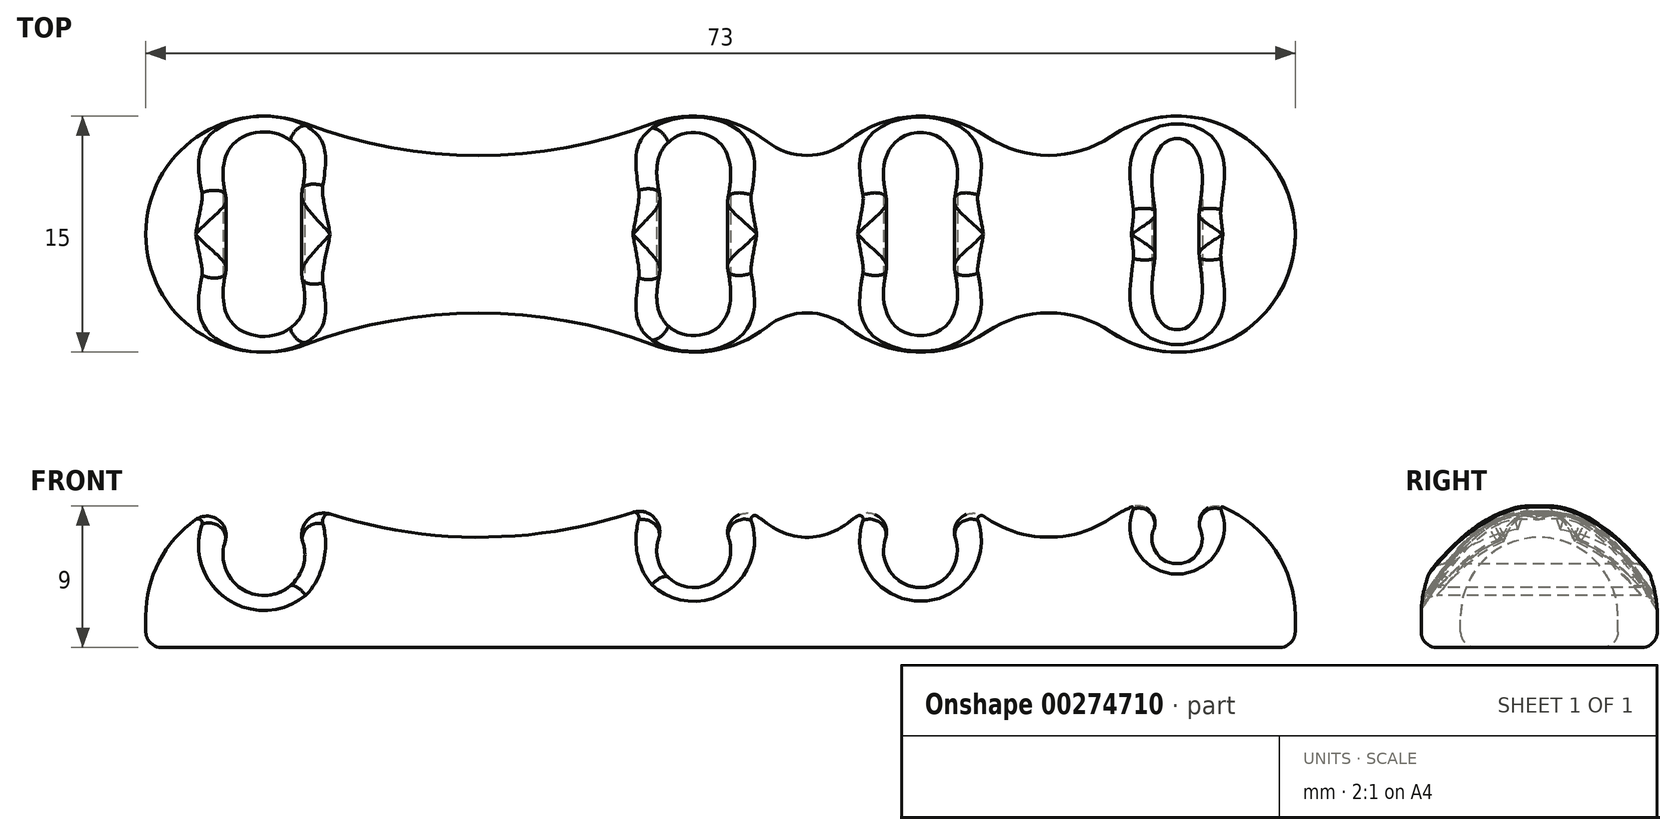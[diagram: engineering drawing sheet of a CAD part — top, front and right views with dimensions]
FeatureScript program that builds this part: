
annotation { "Feature Type Name" : "Feature", "Feature Type Description" : "" }
export const myFeature = defineFeature(function(context is Context, id is Id, definition is map)
    precondition{}
    {
        {
            var Q0;
            Q0=qCreatedBy(makeId("Top.planeOp"),FACE);
            var sketch = newSketch(context, id + "F0", { "sketchPlane" : qUnion([Q0])});
            skArc(sketch, "E0", {"start": v(7.5, 0) * mm, "mid": v(3.51, 6.63) * mm, "end": v(-4.2, 6.2) * mm});
            skArc(sketch, "E1", {"start": v(-55.34, 7.01) * mm, "mid": v(-62.26, 6.17) * mm, "end": v(-65.5, 0) * mm});
            skArc(sketch, "E2", {"start": v(-55.34, 7.01) * mm, "mid": v(-44.35, 5) * mm, "end": v(-33.36, 7.01) * mm});
            skArc(sketch, "E3", {"start": v(-26.05, 5.89) * mm, "mid": v(-23.5, 5) * mm, "end": v(-20.95, 5.89) * mm});
            skArc(sketch, "E4", {"start": v(-12.1, 6.2) * mm, "mid": v(-8.15, 5) * mm, "end": v(-4.2, 6.2) * mm});
            skLineSegment(sketch, "E5", {"start": v(-44.35, 5) * mm, "end": v(-8.15, 5) * mm, "construction": true});
            skLineSegment(sketch, "E6", {"start": v(-65.5, 0) * mm, "end": v(7.5, 0) * mm});
            skArc(sketch, "E7.trimOffspring", {"start": v(-26.05, 5.89) * mm, "mid": v(-29.56, 7.41) * mm, "end": v(-33.36, 7.01) * mm});
            skArc(sketch, "E8.trimOffspring", {"start": v(-12.1, 6.2) * mm, "mid": v(-16.57, 7.5) * mm, "end": v(-20.95, 5.89) * mm});
            skSolve(sketch);
        }
        {
            var Q0;
            Q0=makeQuery(id+"F0.imprint","IMPRINT",FACE,{"disambiguationData":[TD([[makeQuery(id+"F0.imprint","IMPRINT",EDGE,{"derivedFrom":sQuery(id+"F0.wireOp",EDGE,"E0")}),1.0]])]});
            var Q1;
            Q1=sQuery(id+"F0.wireOp",EDGE,"E6");
            revolve(context, id + "F1", {"entities" : qUnion([Q0]), "axis" : qUnion([Q1]), "revolveType" : RevolveType.ONE_DIRECTION, "angle" : 180 * degree});
        }
        {
            var Q0;
            Q0=makeQuery(id+"F1.opRevolve","CAP_FACE",FACE,{"disambiguationData":[OSD([sQuery(id+"F0.wireOp",EDGE,"E0"),sQuery(id+"F0.wireOp",EDGE,"E1"),sQuery(id+"F0.wireOp",EDGE,"E2"),sQuery(id+"F0.wireOp",EDGE,"E3"),sQuery(id+"F0.wireOp",EDGE,"E4"),sQuery(id+"F0.wireOp",EDGE,"E6"),sQuery(id+"F0.wireOp",EDGE,"E7.trimOffspring"),sQuery(id+"F0.wireOp",EDGE,"E8.trimOffspring")])],"isStart":true});
            extrude(context, id + "F2", {"entities" : qUnion([Q0]), "operationType" : NewBodyOperationType.ADD, "depth" : 2 * mm});
        }
        {
            var Q0;
            Q0=makeQuery(id+"F2.opExtrude","CAP_EDGE",EDGE,{"disambiguationData":[OSD([sQuery(id+"F0.wireOp",EDGE,"E1")])],"isStart":false});
            fillet(context, id + "F3", {"entities" : qUnion([Q0]), "radius" : 1 * mm, "tangentPropagation" : true, "allowEdgeOverflow" : false});
        }
        {
            var Q0;
            Q0=qCreatedBy(makeId("Front.planeOp"),FACE);
            var sketch = newSketch(context, id + "F4", { "sketchPlane" : qUnion([Q0])});
            skArc(sketch, "E9", {"start": v(-55.34, 7.01) * mm, "mid": v(-62.26, 6.17) * mm, "end": v(-65.5, 0) * mm});
            skArc(sketch, "E10", {"start": v(-26.05, 5.89) * mm, "mid": v(-29.56, 7.41) * mm, "end": v(-33.36, 7.01) * mm});
            skArc(sketch, "E11", {"start": v(-12.1, 6.2) * mm, "mid": v(-16.57, 7.5) * mm, "end": v(-20.95, 5.89) * mm});
            skArc(sketch, "E12", {"start": v(7.5, 0) * mm, "mid": v(3.51, 6.63) * mm, "end": v(-4.2, 6.2) * mm});
            skArc(sketch, "E13", {"start": v(-60.4, 4.9) * mm, "mid": v(-58, 1.3) * mm, "end": v(-55.6, 4.9) * mm});
            skArc(sketch, "E14", {"start": v(-32.85, 5.1) * mm, "mid": v(-30.7, 1.8) * mm, "end": v(-28.55, 5.1) * mm});
            skArc(sketch, "E15", {"start": v(-18.45, 5.1) * mm, "mid": v(-16.3, 1.8) * mm, "end": v(-14.15, 5.1) * mm});
            skArc(sketch, "E16", {"start": v(-1.4, 5.67) * mm, "mid": v(0, 3.3) * mm, "end": v(1.4, 5.67) * mm});
            skArc(sketch, "E17", {"start": v(-53.79, 6.47) * mm, "mid": v(-55.2, 6.13) * mm, "end": v(-55.53, 4.71) * mm});
            skArc(sketch, "E18", {"start": v(-60.46, 4.73) * mm, "mid": v(-60.9, 6.1) * mm, "end": v(-62.33, 6.12) * mm});
            skLineSegment(sketch, "E19", {"start": v(-55.6, 5.15) * mm, "end": v(-55.6, 3.9) * mm, "construction": true});
            skArc(sketch, "E20", {"start": v(-55.34, 7.01) * mm, "mid": v(-44.35, 5) * mm, "end": v(-33.36, 7.01) * mm});
            skLineSegment(sketch, "E21", {"start": v(-60.4, 5.12) * mm, "end": v(-60.4, 3.9) * mm, "construction": true});
            skArc(sketch, "E22", {"start": v(-32.92, 4.92) * mm, "mid": v(-33.23, 6.26) * mm, "end": v(-34.57, 6.58) * mm});
            skArc(sketch, "E23", {"start": v(-26.7, 6.35) * mm, "mid": v(-28.1, 6.27) * mm, "end": v(-28.48, 4.93) * mm});
            skLineSegment(sketch, "E24", {"start": v(-32.85, 5.34) * mm, "end": v(-32.85, 4.15) * mm, "construction": true});
            skLineSegment(sketch, "E25", {"start": v(-28.55, 5.33) * mm, "end": v(-28.55, 4.15) * mm, "construction": true});
            skArc(sketch, "E26", {"start": v(-18.52, 4.93) * mm, "mid": v(-18.9, 6.27) * mm, "end": v(-20.3, 6.35) * mm});
            skArc(sketch, "E27", {"start": v(-12.3, 6.35) * mm, "mid": v(-13.7, 6.27) * mm, "end": v(-14.08, 4.93) * mm});
            skLineSegment(sketch, "E28", {"start": v(-18.45, 5.33) * mm, "end": v(-18.45, 4.15) * mm, "construction": true});
            skLineSegment(sketch, "E29", {"start": v(-14.15, 5.33) * mm, "end": v(-14.15, 4.15) * mm, "construction": true});
            skArc(sketch, "E30", {"start": v(-1.48, 5.5) * mm, "mid": v(-1.72, 6.69) * mm, "end": v(-2.9, 6.92) * mm});
            skArc(sketch, "E31", {"start": v(1.48, 5.5) * mm, "mid": v(1.72, 6.69) * mm, "end": v(2.9, 6.92) * mm});
            skLineSegment(sketch, "E32", {"start": v(-1.4, 5.92) * mm, "end": v(-1.4, 4.9) * mm, "construction": true});
            skLineSegment(sketch, "E33", {"start": v(1.4, 5.92) * mm, "end": v(1.4, 4.9) * mm, "construction": true});
            skSolve(sketch);
        }
        {
            var Q0;
            Q0 = qSketchRegion(id + "F4", true);
            extrude(context, id + "F5", {"entities" : qUnion([Q0]), "operationType" : NewBodyOperationType.REMOVE, "endBound" : BoundingType.SYMMETRIC, "oppositeDirection" : true, "depth" : 25 * mm});
        }
        {
            var Q0;
            Q0=makeQuery(id+"F5.boolean.opBoolean","COPY",FACE,{"derivedFrom":makeQuery(id+"F5.opExtrude","SWEPT_FACE",FACE,{"disambiguationData":[OSD([sQuery(id+"F4.wireOp",EDGE,"E16")])]})});
            var Q1;
            Q1=makeQuery(id+"F5.boolean.opBoolean","COPY",FACE,{"derivedFrom":makeQuery(id+"F5.opExtrude","SWEPT_FACE",FACE,{"disambiguationData":[OSD([sQuery(id+"F4.wireOp",EDGE,"E15")])]})});
            var Q2;
            Q2=makeQuery(id+"F5.boolean.opBoolean","COPY",FACE,{"derivedFrom":makeQuery(id+"F5.opExtrude","SWEPT_FACE",FACE,{"disambiguationData":[OSD([sQuery(id+"F4.wireOp",EDGE,"E14")])]})});
            var Q3;
            Q3=makeQuery(id+"F5.boolean.opBoolean","COPY",FACE,{"derivedFrom":makeQuery(id+"F5.opExtrude","SWEPT_FACE",FACE,{"disambiguationData":[OSD([sQuery(id+"F4.wireOp",EDGE,"E13")])]})});
            fillet(context, id + "F6", {"entities" : qUnion([Q0, Q1, Q2, Q3]), "radius" : 1 * mm, "tangentPropagation" : true, "allowEdgeOverflow" : false});
        }
    });
